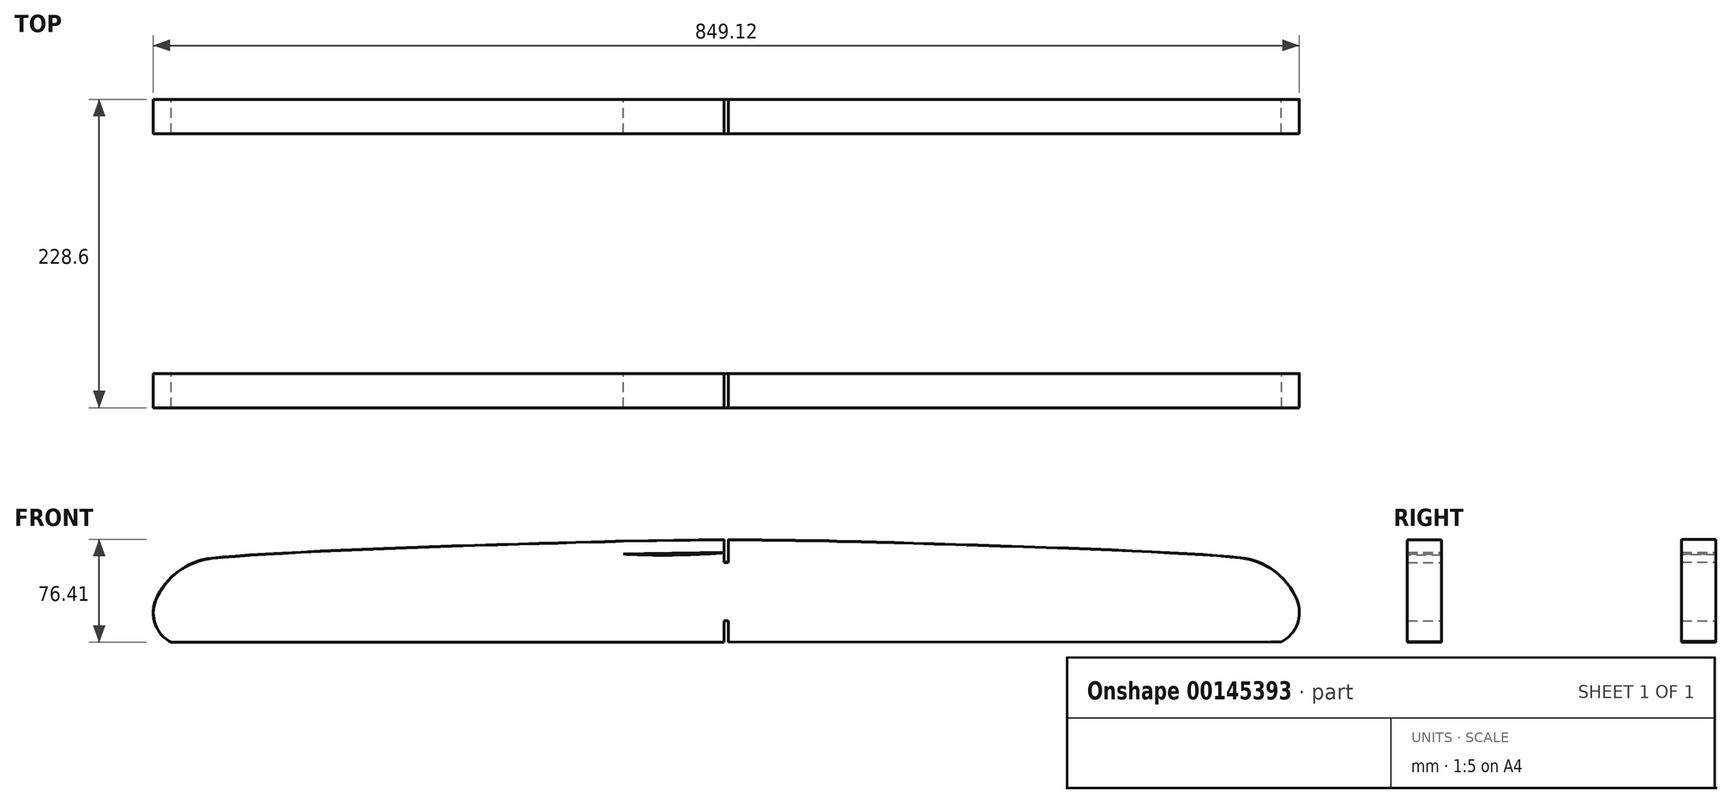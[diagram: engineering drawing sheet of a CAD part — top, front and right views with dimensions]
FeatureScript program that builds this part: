
annotation { "Feature Type Name" : "Feature", "Feature Type Description" : "" }
export const myFeature = defineFeature(function(context is Context, id is Id, definition is map)
    precondition{}
    {
        {
            var Q0;
            Q0=qCreatedBy(makeId("Front.planeOp"),FACE);
            var sketch = newSketch(context, id + "F0", { "sketchPlane" : qUnion([Q0])});
            skLineSegment(sketch, "E0", {"start": v(-1.62, 0) * mm, "end": v(-76.2, 0) * mm});
            skLineSegment(sketch, "E1", {"start": v(-76.2, 0) * mm, "end": v(-228.6, 0) * mm});
            skLineSegment(sketch, "E2", {"start": v(-228.6, 0) * mm, "end": v(-381, 0) * mm});
            skFitSpline(sketch, "E3", {"points": [v(-0.04, 76.2) * mm, v(-76.2, 74.93) * mm, v(-228.6, 70.3) * mm, v(-381, 62.23) * mm], "startDerivative": vector(-875.17, -14.6) * mm, "endDerivative": vector(-228.23, -24.36) * mm});
            skArc(sketch, "E4", {"start": v(-381, 62.23) * mm, "mid": v(-406.09, 52.38) * mm, "end": v(-422.65, 31.11) * mm});
            skPoint(sketch, "E4.endSnap0", {"position": v(-381, 31.12) * mm});
            skArc(sketch, "E5", {"start": v(-422.65, 31.12) * mm, "mid": v(-423.01, 13.32) * mm, "end": v(-411.2, 0) * mm});
            skFitSpline(sketch, "E6.0", {"points": [v(-76.52, 65.43) * mm, v(-70.1, 65.16) * mm, v(-57.25, 64.76) * mm, v(-41.12, 64.7) * mm, v(-28.19, 64.96) * mm, v(-18.47, 65.34) * mm, v(-10.37, 65.82) * mm, v(-3.88, 66.3) * mm, v(1, 66.73) * mm, v(5.86, 67.2) * mm, v(12.3, 67.89) * mm, v(20.3, 68.82) * mm, v(29.82, 69.97) * mm, v(42.38, 71.42) * mm, v(57.87, 72.87) * mm, v(70.02, 73.2) * mm, v(76.04, 73.04) * mm]});
            skFitSpline(sketch, "E6.1", {"points": [v(0.12, 66.69) * mm, v(-18.11, 66.39) * mm, v(-44.38, 65.96) * mm, v(-59.59, 65.74) * mm, v(-65.88, 65.64) * mm, v(-68.33, 65.6) * mm, v(-69.98, 65.57) * mm, v(-71.23, 65.54) * mm, v(-72.65, 65.5) * mm, v(-74.08, 65.47) * mm, v(-75.46, 65.43) * mm, v(-77, 65.4) * mm, v(-79.29, 65.33) * mm, v(-82.55, 65.25) * mm, v(-86.3, 65.15) * mm, v(-90.51, 65.03) * mm, v(-96.73, 64.87) * mm, v(-105.53, 64.62) * mm, v(-117.56, 64.29) * mm, v(-135.27, 63.78) * mm, v(-160.04, 63.05) * mm, v(-186.94, 62.2) * mm, v(-208.92, 61.48) * mm, v(-225.43, 60.9) * mm, v(-241.75, 60.32) * mm, v(-263.12, 59.5) * mm, v(-288.84, 58.44) * mm, v(-317.36, 57.1) * mm, v(-342.75, 55.7) * mm, v(-360.64, 54.5) * mm, v(-372.58, 53.51) * mm, v(-377.68, 53.02) * mm, v(-379.99, 52.77) * mm]});
            skArc(sketch, "E6.3", {"start": v(-379.99, 52.77) * mm, "mid": v(-400.3, 45.13) * mm, "end": v(-413.96, 28.27) * mm});
            skArc(sketch, "E6.4", {"start": v(-413.96, 28.27) * mm, "mid": v(-414.5, 18.38) * mm, "end": v(-408.72, 10.33) * mm});
            skLineSegment(sketch, "E6.8", {"start": v(-408.72, 10.33) * mm, "end": v(-244.49, 10) * mm});
            skLineSegment(sketch, "E7.0", {"start": v(-13.13, 15.89) * mm, "end": v(-13.13, 59.3) * mm});
            skLineSegment(sketch, "E8.trimOffspring", {"start": v(0, 0.8) * mm, "end": v(-0.06, 0.8) * mm});
            skLineSegment(sketch, "E9", {"start": v(-76.2, 74.93) * mm, "end": v(-1.62, 76.17) * mm});
            skLineSegment(sketch, "E10", {"start": v(-76.12, 65.41) * mm, "end": v(-19.5, 65.64) * mm});
            skLineSegment(sketch, "E11.MirrorCS", {"start": v(411.2, 0.39) * mm, "end": v(1.55, 0) * mm});
            skArc(sketch, "E12.MirrorCS", {"start": v(422.62, 31.51) * mm, "mid": v(423, 13.72) * mm, "end": v(411.2, 0.39) * mm});
            skArc(sketch, "E13.MirrorCS", {"start": v(380.94, 62.59) * mm, "mid": v(406.04, 52.77) * mm, "end": v(422.62, 31.51) * mm});
            skFitSpline(sketch, "E14.MirrorCS", {"points": [v(-0.04, 76.2) * mm, v(76.13, 75) * mm, v(228.53, 70.52) * mm, v(380.94, 62.59) * mm], "startDerivative": vector(875.19, -13.77) * mm, "endDerivative": vector(228.25, -24.14) * mm});
            skLineSegment(sketch, "E15.MirrorCS", {"start": v(76.13, 75) * mm, "end": v(1.55, 76.18) * mm});
            skLineSegment(sketch, "E16", {"start": v(-411.2, 0) * mm, "end": v(-381, 0) * mm});
            skLineSegment(sketch, "E17.0", {"start": v(-219, 16.28) * mm, "end": v(-219, 55) * mm});
            skLineSegment(sketch, "E18.MirrorCS", {"start": v(-238.13, 16.35) * mm, "end": v(-238.13, 53.85) * mm});
            skFitSpline(sketch, "E19.trimOffspring", {"points": [v(0.12, 66.69) * mm, v(-18.11, 66.39) * mm, v(-44.38, 65.96) * mm, v(-59.59, 65.74) * mm, v(-65.88, 65.64) * mm, v(-68.33, 65.6) * mm, v(-69.98, 65.57) * mm, v(-71.23, 65.54) * mm, v(-72.65, 65.5) * mm, v(-74.08, 65.47) * mm, v(-75.46, 65.43) * mm, v(-77, 65.4) * mm, v(-79.29, 65.33) * mm, v(-82.55, 65.25) * mm, v(-86.3, 65.15) * mm, v(-90.51, 65.03) * mm, v(-96.73, 64.87) * mm, v(-105.53, 64.62) * mm, v(-117.56, 64.29) * mm, v(-135.27, 63.78) * mm, v(-160.04, 63.05) * mm, v(-186.94, 62.2) * mm, v(-208.92, 61.48) * mm, v(-225.43, 60.9) * mm, v(-241.75, 60.32) * mm, v(-263.12, 59.5) * mm, v(-288.84, 58.44) * mm, v(-317.36, 57.1) * mm, v(-342.75, 55.7) * mm, v(-360.64, 54.5) * mm, v(-372.58, 53.51) * mm, v(-377.68, 53.02) * mm, v(-379.99, 52.77) * mm]});
            skLineSegment(sketch, "E20.trimOffspring", {"start": v(-212.66, 9.93) * mm, "end": v(-19.5, 9.54) * mm});
            skFitSpline(sketch, "E21.MirrorCS", {"points": [v(-0.12, 66.69) * mm, v(18.11, 66.39) * mm, v(44.38, 65.96) * mm, v(59.59, 65.74) * mm, v(65.88, 65.64) * mm, v(68.33, 65.6) * mm, v(69.98, 65.57) * mm, v(71.23, 65.54) * mm, v(72.65, 65.5) * mm, v(74.08, 65.47) * mm, v(75.46, 65.43) * mm, v(77, 65.4) * mm, v(79.29, 65.33) * mm, v(82.55, 65.25) * mm, v(86.3, 65.15) * mm, v(90.51, 65.03) * mm, v(96.73, 64.87) * mm, v(105.53, 64.62) * mm, v(117.56, 64.29) * mm, v(135.27, 63.78) * mm, v(160.04, 63.05) * mm, v(186.94, 62.2) * mm, v(208.92, 61.48) * mm, v(225.43, 60.9) * mm, v(241.75, 60.32) * mm, v(263.12, 59.5) * mm, v(288.84, 58.44) * mm, v(317.36, 57.1) * mm, v(342.75, 55.7) * mm, v(360.64, 54.5) * mm, v(372.58, 53.51) * mm, v(377.68, 53.02) * mm, v(379.99, 52.77) * mm]});
            skArc(sketch, "E22.MirrorCS", {"start": v(379.99, 52.77) * mm, "mid": v(400.3, 45.13) * mm, "end": v(413.96, 28.27) * mm});
            skArc(sketch, "E23.MirrorCS", {"start": v(413.96, 28.27) * mm, "mid": v(414.5, 18.38) * mm, "end": v(408.72, 10.33) * mm});
            skLineSegment(sketch, "E24.MirrorCS", {"start": v(408.72, 10.33) * mm, "end": v(244.49, 10) * mm});
            skLineSegment(sketch, "E25.MirrorCS", {"start": v(238.13, 16.35) * mm, "end": v(238.13, 53.85) * mm});
            skLineSegment(sketch, "E26.MirrorCS", {"start": v(219, 16.28) * mm, "end": v(219, 55) * mm});
            skFitSpline(sketch, "E27.MirrorCS", {"points": [v(-0.12, 66.69) * mm, v(18.11, 66.39) * mm, v(44.38, 65.96) * mm, v(59.59, 65.74) * mm, v(65.88, 65.64) * mm, v(68.33, 65.6) * mm, v(69.98, 65.57) * mm, v(71.23, 65.54) * mm, v(72.65, 65.5) * mm, v(74.08, 65.47) * mm, v(75.46, 65.43) * mm, v(77, 65.4) * mm, v(79.29, 65.33) * mm, v(82.55, 65.25) * mm, v(86.3, 65.15) * mm, v(90.51, 65.03) * mm, v(96.73, 64.87) * mm, v(105.53, 64.62) * mm, v(117.56, 64.29) * mm, v(135.27, 63.78) * mm, v(160.04, 63.05) * mm, v(186.94, 62.2) * mm, v(208.92, 61.48) * mm, v(225.43, 60.9) * mm, v(241.75, 60.32) * mm, v(263.12, 59.5) * mm, v(288.84, 58.44) * mm, v(317.36, 57.1) * mm, v(342.75, 55.7) * mm, v(360.64, 54.5) * mm, v(372.58, 53.51) * mm, v(377.68, 53.02) * mm, v(379.99, 52.77) * mm]});
            skLineSegment(sketch, "E28.MirrorCS", {"start": v(76.12, 65.41) * mm, "end": v(19.5, 65.64) * mm});
            skLineSegment(sketch, "E29.MirrorCS", {"start": v(13.13, 15.89) * mm, "end": v(13.13, 59.3) * mm});
            skLineSegment(sketch, "E30.MirrorCS", {"start": v(212.66, 9.93) * mm, "end": v(19.5, 9.54) * mm});
            skPoint(sketch, "E31.visualSharp", {"position": v(13.13, 9.52) * mm});
            skArc(sketch, "E31.filletArc", {"start": v(13.13, 15.89) * mm, "mid": v(15, 11.4) * mm, "end": v(19.5, 9.54) * mm});
            skPoint(sketch, "E32.visualSharp", {"position": v(13.13, 65.67) * mm});
            skArc(sketch, "E32.filletArc", {"start": v(19.5, 65.64) * mm, "mid": v(15, 63.8) * mm, "end": v(13.13, 59.3) * mm});
            skPoint(sketch, "E33.visualSharp", {"position": v(219, 61.13) * mm});
            skArc(sketch, "E33.filletArc", {"start": v(219, 55) * mm, "mid": v(217.2, 59.4) * mm, "end": v(212.86, 61.34) * mm});
            skPoint(sketch, "E34.visualSharp", {"position": v(219, 9.95) * mm});
            skArc(sketch, "E34.filletArc", {"start": v(212.66, 9.93) * mm, "mid": v(217.14, 11.8) * mm, "end": v(219, 16.28) * mm});
            skLineSegment(sketch, "E35", {"start": v(76.12, 65.41) * mm, "end": v(76.2, 65.41) * mm});
            skPoint(sketch, "E36.visualSharp", {"position": v(238.13, 60.44) * mm});
            skArc(sketch, "E36.filletArc", {"start": v(244.71, 60.2) * mm, "mid": v(240.07, 58.43) * mm, "end": v(238.13, 53.85) * mm});
            skPoint(sketch, "E37.visualSharp", {"position": v(238.13, 9.98) * mm});
            skArc(sketch, "E37.filletArc", {"start": v(238.13, 16.35) * mm, "mid": v(239.99, 11.85) * mm, "end": v(244.49, 10) * mm});
            skPoint(sketch, "E38.visualSharp", {"position": v(-13.13, 65.67) * mm});
            skArc(sketch, "E38.filletArc", {"start": v(-13.13, 59.3) * mm, "mid": v(-15, 63.8) * mm, "end": v(-19.5, 65.64) * mm});
            skPoint(sketch, "E39.visualSharp", {"position": v(-13.13, 9.52) * mm});
            skArc(sketch, "E39.filletArc", {"start": v(-19.5, 9.54) * mm, "mid": v(-15, 11.4) * mm, "end": v(-13.13, 15.89) * mm});
            skPoint(sketch, "E40.visualSharp", {"position": v(-219, 61.13) * mm});
            skArc(sketch, "E40.filletArc", {"start": v(-212.86, 61.34) * mm, "mid": v(-217.2, 59.4) * mm, "end": v(-219, 55) * mm});
            skPoint(sketch, "E41.visualSharp", {"position": v(-219, 9.95) * mm});
            skArc(sketch, "E41.filletArc", {"start": v(-219, 16.28) * mm, "mid": v(-217.14, 11.8) * mm, "end": v(-212.66, 9.93) * mm});
            skPoint(sketch, "E42.visualSharp", {"position": v(-238.13, 60.44) * mm});
            skArc(sketch, "E42.filletArc", {"start": v(-238.13, 53.85) * mm, "mid": v(-240.07, 58.43) * mm, "end": v(-244.71, 60.2) * mm});
            skPoint(sketch, "E43.visualSharp", {"position": v(-238.13, 9.98) * mm});
            skArc(sketch, "E43.filletArc", {"start": v(-244.49, 10) * mm, "mid": v(-239.99, 11.85) * mm, "end": v(-238.13, 16.35) * mm});
            skLineSegment(sketch, "E44.left", {"start": v(1.55, 0) * mm, "end": v(1.55, 15.89) * mm});
            skLineSegment(sketch, "E44.right", {"start": v(-1.62, 0) * mm, "end": v(-1.62, 15.89) * mm});
            skLineSegment(sketch, "E45", {"start": v(-1.62, 59.3) * mm, "end": v(1.55, 59.3) * mm});
            skLineSegment(sketch, "E46", {"start": v(-1.62, 15.89) * mm, "end": v(1.55, 15.89) * mm});
            skPoint(sketch, "E47.orphan", {"position": v(-3.05, 15.89) * mm});
            skLineSegment(sketch, "E48.trimOffspring", {"start": v(1.55, 59.3) * mm, "end": v(1.55, 76.18) * mm});
            skLineSegment(sketch, "E49.trimOffspring", {"start": v(-1.62, 59.3) * mm, "end": v(-1.62, 76.17) * mm});
            skPoint(sketch, "E44.bottom.end.orphan", {"position": v(-1.62, -31.54) * mm});
            skPoint(sketch, "E44.bottom.start.orphan", {"position": v(1.55, -31.54) * mm});
            skPoint(sketch, "E44.top.end.orphan", {"position": v(-1.62, 183.94) * mm});
            skPoint(sketch, "E44.top.start.orphan", {"position": v(1.55, 183.94) * mm});
            skSolve(sketch);
        }
        {
            var Q0;
            Q0=makeQuery(id+"F0.imprint","IMPRINT",FACE,{"disambiguationData":[TD([[makeQuery(id+"F0.imprint","IMPRINT",EDGE,{"derivedFrom":sQuery(id+"F0.wireOp",EDGE,"E0")}),-1.0]])]});
            extrude(context, id + "F1", {"entities" : qUnion([Q0]), "depth" : 25.4 * mm});
        }
        {
            var Q0;
            Q0=qCreatedBy(makeId("Front.planeOp"),FACE);
            cPlane(context, id + "F2", {"entities" : qUnion([Q0]), "cplaneType" : CPlaneType.OFFSET, "offset" : 203.2 * mm, "width" : 152.4 * mm, "height" : 152.4 * mm});
        }
        {
            var Q0;
            Q0=qCreatedBy(id+"F2.planeOp",FACE);
            var sketch = newSketch(context, id + "F3", { "sketchPlane" : qUnion([Q0])});
            skLineSegment(sketch, "E50", {"start": v(-1.51, -0.23) * mm, "end": v(-76.1, -0.23) * mm});
            skLineSegment(sketch, "E51", {"start": v(-76.1, -0.23) * mm, "end": v(-228.5, -0.23) * mm});
            skLineSegment(sketch, "E52", {"start": v(-228.5, -0.23) * mm, "end": v(-380.9, -0.23) * mm});
            skFitSpline(sketch, "E53", {"points": [v(0.07, 75.97) * mm, v(-76.1, 74.7) * mm, v(-228.5, 70.07) * mm, v(-380.9, 62) * mm], "startDerivative": vector(-875.17, -14.6) * mm, "endDerivative": vector(-228.23, -24.36) * mm});
            skArc(sketch, "E54", {"start": v(-380.9, 62) * mm, "mid": v(-405.98, 52.15) * mm, "end": v(-422.54, 30.88) * mm});
            skPoint(sketch, "E54.endSnap0", {"position": v(-380.9, 30.88) * mm});
            skArc(sketch, "E55", {"start": v(-422.54, 30.88) * mm, "mid": v(-422.9, 13.08) * mm, "end": v(-411.1, -0.23) * mm});
            skFitSpline(sketch, "E56.0", {"points": [v(-76.41, 65.2) * mm, v(-70, 64.93) * mm, v(-57.15, 64.52) * mm, v(-41.01, 64.46) * mm, v(-28.08, 64.73) * mm, v(-18.36, 65.1) * mm, v(-10.26, 65.59) * mm, v(-3.77, 66.07) * mm, v(1.1, 66.5) * mm, v(5.96, 66.97) * mm, v(12.41, 67.66) * mm, v(20.41, 68.59) * mm, v(29.93, 69.74) * mm, v(42.5, 71.2) * mm, v(57.97, 72.64) * mm, v(70.13, 72.96) * mm, v(76.15, 72.8) * mm]});
            skFitSpline(sketch, "E56.1", {"points": [v(0.23, 66.46) * mm, v(-18, 66.15) * mm, v(-44.27, 65.73) * mm, v(-59.48, 65.5) * mm, v(-65.77, 65.41) * mm, v(-68.22, 65.37) * mm, v(-69.88, 65.34) * mm, v(-71.13, 65.3) * mm, v(-72.54, 65.27) * mm, v(-73.97, 65.24) * mm, v(-75.35, 65.2) * mm, v(-76.9, 65.16) * mm, v(-79.18, 65.1) * mm, v(-82.44, 65.01) * mm, v(-86.19, 64.91) * mm, v(-90.4, 64.8) * mm, v(-96.62, 64.63) * mm, v(-105.42, 64.39) * mm, v(-117.45, 64.05) * mm, v(-135.16, 63.55) * mm, v(-159.93, 62.82) * mm, v(-186.83, 61.97) * mm, v(-208.81, 61.24) * mm, v(-225.32, 60.67) * mm, v(-241.64, 60.08) * mm, v(-263, 59.27) * mm, v(-288.73, 58.2) * mm, v(-317.25, 56.87) * mm, v(-342.64, 55.47) * mm, v(-360.54, 54.26) * mm, v(-372.47, 53.28) * mm, v(-377.57, 52.78) * mm, v(-379.88, 52.54) * mm]});
            skArc(sketch, "E56.3", {"start": v(-379.88, 52.54) * mm, "mid": v(-400.2, 44.9) * mm, "end": v(-413.86, 28.03) * mm});
            skArc(sketch, "E56.4", {"start": v(-413.86, 28.03) * mm, "mid": v(-414.4, 18.14) * mm, "end": v(-408.61, 10.1) * mm});
            skLineSegment(sketch, "E56.8", {"start": v(-408.61, 10.1) * mm, "end": v(-244.38, 9.76) * mm});
            skLineSegment(sketch, "E57.0", {"start": v(-13.02, 15.65) * mm, "end": v(-13.02, 59.06) * mm});
            skLineSegment(sketch, "E58.trimOffspring", {"start": v(0.1, 0.56) * mm, "end": v(0.05, 0.56) * mm});
            skLineSegment(sketch, "E59", {"start": v(-76.1, 74.7) * mm, "end": v(-1.51, 75.94) * mm});
            skLineSegment(sketch, "E60", {"start": v(-76.02, 65.18) * mm, "end": v(-19.4, 65.4) * mm});
            skLineSegment(sketch, "E61.MirrorCS", {"start": v(411.3, 0.15) * mm, "end": v(1.66, -0.23) * mm});
            skArc(sketch, "E62.MirrorCS", {"start": v(422.73, 31.28) * mm, "mid": v(423.11, 13.48) * mm, "end": v(411.3, 0.15) * mm});
            skArc(sketch, "E63.MirrorCS", {"start": v(381.05, 62.36) * mm, "mid": v(406.15, 52.53) * mm, "end": v(422.73, 31.28) * mm});
            skFitSpline(sketch, "E64.MirrorCS", {"points": [v(0.07, 75.97) * mm, v(76.24, 74.77) * mm, v(228.64, 70.29) * mm, v(381.05, 62.36) * mm], "startDerivative": vector(875.19, -13.77) * mm, "endDerivative": vector(228.25, -24.14) * mm});
            skLineSegment(sketch, "E65.MirrorCS", {"start": v(76.24, 74.77) * mm, "end": v(1.66, 75.94) * mm});
            skLineSegment(sketch, "E66", {"start": v(-411.1, -0.23) * mm, "end": v(-380.9, -0.23) * mm});
            skLineSegment(sketch, "E67.0", {"start": v(-218.88, 16.05) * mm, "end": v(-218.88, 54.76) * mm});
            skLineSegment(sketch, "E68.MirrorCS", {"start": v(-238.02, 16.11) * mm, "end": v(-238.02, 53.62) * mm});
            skFitSpline(sketch, "E69.trimOffspring", {"points": [v(0.23, 66.46) * mm, v(-18, 66.15) * mm, v(-44.27, 65.73) * mm, v(-59.48, 65.5) * mm, v(-65.77, 65.41) * mm, v(-68.22, 65.37) * mm, v(-69.88, 65.34) * mm, v(-71.13, 65.3) * mm, v(-72.54, 65.27) * mm, v(-73.97, 65.24) * mm, v(-75.35, 65.2) * mm, v(-76.9, 65.16) * mm, v(-79.18, 65.1) * mm, v(-82.44, 65.01) * mm, v(-86.19, 64.91) * mm, v(-90.4, 64.8) * mm, v(-96.62, 64.63) * mm, v(-105.42, 64.39) * mm, v(-117.45, 64.05) * mm, v(-135.16, 63.55) * mm, v(-159.93, 62.82) * mm, v(-186.83, 61.97) * mm, v(-208.81, 61.24) * mm, v(-225.32, 60.67) * mm, v(-241.64, 60.08) * mm, v(-263, 59.27) * mm, v(-288.73, 58.2) * mm, v(-317.25, 56.87) * mm, v(-342.64, 55.47) * mm, v(-360.54, 54.26) * mm, v(-372.47, 53.28) * mm, v(-377.57, 52.78) * mm, v(-379.88, 52.54) * mm]});
            skLineSegment(sketch, "E70.trimOffspring", {"start": v(-212.55, 9.7) * mm, "end": v(-19.39, 9.3) * mm});
            skFitSpline(sketch, "E71.MirrorCS", {"points": [v(-0.01, 66.46) * mm, v(18.22, 66.15) * mm, v(44.5, 65.73) * mm, v(59.7, 65.5) * mm, v(65.99, 65.41) * mm, v(68.44, 65.37) * mm, v(70.1, 65.34) * mm, v(71.34, 65.3) * mm, v(72.76, 65.27) * mm, v(74.2, 65.24) * mm, v(75.56, 65.2) * mm, v(77.12, 65.16) * mm, v(79.4, 65.1) * mm, v(82.66, 65.01) * mm, v(86.4, 64.91) * mm, v(90.62, 64.8) * mm, v(96.83, 64.63) * mm, v(105.64, 64.39) * mm, v(117.67, 64.05) * mm, v(135.38, 63.55) * mm, v(160.15, 62.82) * mm, v(187.05, 61.97) * mm, v(209.03, 61.24) * mm, v(225.54, 60.67) * mm, v(241.86, 60.08) * mm, v(263.22, 59.27) * mm, v(288.95, 58.2) * mm, v(317.47, 56.87) * mm, v(342.86, 55.47) * mm, v(360.75, 54.26) * mm, v(372.69, 53.28) * mm, v(377.79, 52.78) * mm, v(380.1, 52.54) * mm]});
            skArc(sketch, "E72.MirrorCS", {"start": v(380.1, 52.54) * mm, "mid": v(400.4, 44.9) * mm, "end": v(414.07, 28.03) * mm});
            skArc(sketch, "E73.MirrorCS", {"start": v(414.07, 28.03) * mm, "mid": v(414.62, 18.14) * mm, "end": v(408.83, 10.1) * mm});
            skLineSegment(sketch, "E74.MirrorCS", {"start": v(408.83, 10.1) * mm, "end": v(244.6, 9.76) * mm});
            skLineSegment(sketch, "E75.MirrorCS", {"start": v(238.23, 16.11) * mm, "end": v(238.23, 53.62) * mm});
            skLineSegment(sketch, "E76.MirrorCS", {"start": v(219.1, 16.05) * mm, "end": v(219.1, 54.76) * mm});
            skFitSpline(sketch, "E77.MirrorCS", {"points": [v(-0.01, 66.46) * mm, v(18.22, 66.15) * mm, v(44.5, 65.73) * mm, v(59.7, 65.5) * mm, v(65.99, 65.41) * mm, v(68.44, 65.37) * mm, v(70.1, 65.34) * mm, v(71.34, 65.3) * mm, v(72.76, 65.27) * mm, v(74.2, 65.24) * mm, v(75.56, 65.2) * mm, v(77.12, 65.16) * mm, v(79.4, 65.1) * mm, v(82.66, 65.01) * mm, v(86.4, 64.91) * mm, v(90.62, 64.8) * mm, v(96.83, 64.63) * mm, v(105.64, 64.39) * mm, v(117.67, 64.05) * mm, v(135.38, 63.55) * mm, v(160.15, 62.82) * mm, v(187.05, 61.97) * mm, v(209.03, 61.24) * mm, v(225.54, 60.67) * mm, v(241.86, 60.08) * mm, v(263.22, 59.27) * mm, v(288.95, 58.2) * mm, v(317.47, 56.87) * mm, v(342.86, 55.47) * mm, v(360.75, 54.26) * mm, v(372.69, 53.28) * mm, v(377.79, 52.78) * mm, v(380.1, 52.54) * mm]});
            skLineSegment(sketch, "E78.MirrorCS", {"start": v(76.23, 65.18) * mm, "end": v(19.62, 65.4) * mm});
            skLineSegment(sketch, "E79.MirrorCS", {"start": v(13.24, 15.65) * mm, "end": v(13.24, 59.06) * mm});
            skLineSegment(sketch, "E80.MirrorCS", {"start": v(212.76, 9.7) * mm, "end": v(19.6, 9.3) * mm});
            skPoint(sketch, "E81.visualSharp", {"position": v(13.24, 9.3) * mm});
            skArc(sketch, "E81.filletArc", {"start": v(13.24, 15.65) * mm, "mid": v(15.1, 11.16) * mm, "end": v(19.6, 9.3) * mm});
            skPoint(sketch, "E82.visualSharp", {"position": v(13.24, 65.43) * mm});
            skArc(sketch, "E82.filletArc", {"start": v(19.62, 65.4) * mm, "mid": v(15.1, 63.56) * mm, "end": v(13.24, 59.06) * mm});
            skPoint(sketch, "E83.visualSharp", {"position": v(219.1, 60.9) * mm});
            skArc(sketch, "E83.filletArc", {"start": v(219.1, 54.76) * mm, "mid": v(217.32, 59.17) * mm, "end": v(212.97, 61.1) * mm});
            skPoint(sketch, "E84.visualSharp", {"position": v(219.1, 9.71) * mm});
            skArc(sketch, "E84.filletArc", {"start": v(212.76, 9.7) * mm, "mid": v(217.25, 11.56) * mm, "end": v(219.1, 16.05) * mm});
            skLineSegment(sketch, "E85", {"start": v(76.23, 65.18) * mm, "end": v(76.3, 65.18) * mm});
            skPoint(sketch, "E86.visualSharp", {"position": v(238.23, 60.21) * mm});
            skArc(sketch, "E86.filletArc", {"start": v(244.82, 59.97) * mm, "mid": v(240.18, 58.2) * mm, "end": v(238.23, 53.62) * mm});
            skPoint(sketch, "E87.visualSharp", {"position": v(238.23, 9.75) * mm});
            skArc(sketch, "E87.filletArc", {"start": v(238.23, 16.11) * mm, "mid": v(240.1, 11.62) * mm, "end": v(244.6, 9.76) * mm});
            skPoint(sketch, "E88.visualSharp", {"position": v(-13.02, 65.43) * mm});
            skArc(sketch, "E88.filletArc", {"start": v(-13.02, 59.06) * mm, "mid": v(-14.9, 63.56) * mm, "end": v(-19.4, 65.4) * mm});
            skPoint(sketch, "E89.visualSharp", {"position": v(-13.02, 9.3) * mm});
            skArc(sketch, "E89.filletArc", {"start": v(-19.39, 9.3) * mm, "mid": v(-14.89, 11.16) * mm, "end": v(-13.02, 15.65) * mm});
            skPoint(sketch, "E90.visualSharp", {"position": v(-218.88, 60.9) * mm});
            skArc(sketch, "E90.filletArc", {"start": v(-212.75, 61.1) * mm, "mid": v(-217.1, 59.17) * mm, "end": v(-218.88, 54.76) * mm});
            skPoint(sketch, "E91.visualSharp", {"position": v(-218.88, 9.71) * mm});
            skArc(sketch, "E91.filletArc", {"start": v(-218.88, 16.05) * mm, "mid": v(-217.03, 11.56) * mm, "end": v(-212.55, 9.7) * mm});
            skPoint(sketch, "E92.visualSharp", {"position": v(-238.02, 60.21) * mm});
            skArc(sketch, "E92.filletArc", {"start": v(-238.02, 53.62) * mm, "mid": v(-239.96, 58.2) * mm, "end": v(-244.6, 59.97) * mm});
            skPoint(sketch, "E93.visualSharp", {"position": v(-238.02, 9.75) * mm});
            skArc(sketch, "E93.filletArc", {"start": v(-244.38, 9.76) * mm, "mid": v(-239.88, 11.62) * mm, "end": v(-238.02, 16.11) * mm});
            skLineSegment(sketch, "E94.left", {"start": v(1.66, -0.23) * mm, "end": v(1.66, 15.65) * mm});
            skLineSegment(sketch, "E94.right", {"start": v(-1.51, -0.23) * mm, "end": v(-1.51, 15.65) * mm});
            skLineSegment(sketch, "E95", {"start": v(-1.51, 59.06) * mm, "end": v(1.66, 59.06) * mm});
            skLineSegment(sketch, "E96", {"start": v(-1.51, 15.65) * mm, "end": v(1.66, 15.65) * mm});
            skPoint(sketch, "E97.orphan", {"position": v(-2.95, 15.65) * mm});
            skLineSegment(sketch, "E98.trimOffspring", {"start": v(1.66, 59.06) * mm, "end": v(1.66, 75.94) * mm});
            skLineSegment(sketch, "E99.trimOffspring", {"start": v(-1.51, 59.06) * mm, "end": v(-1.51, 75.94) * mm});
            skPoint(sketch, "E94.bottom.end.orphan", {"position": v(-1.51, -31.78) * mm});
            skPoint(sketch, "E94.bottom.start.orphan", {"position": v(1.66, -31.78) * mm});
            skPoint(sketch, "E94.top.end.orphan", {"position": v(-1.51, 183.7) * mm});
            skPoint(sketch, "E94.top.start.orphan", {"position": v(1.66, 183.7) * mm});
            skSolve(sketch);
        }
        {
            var Q0;
            Q0=makeQuery(id+"F3.imprint","IMPRINT",FACE,{"disambiguationData":[TD([[makeQuery(id+"F3.imprint","IMPRINT",EDGE,{"derivedFrom":sQuery(id+"F3.wireOp",EDGE,"E50")}),-1.0]])]});
            extrude(context, id + "F4", {"entities" : qUnion([Q0]), "depth" : 25.4 * mm});
        }
    });
